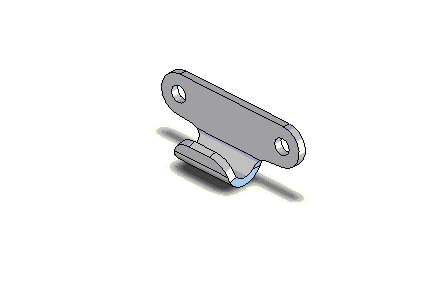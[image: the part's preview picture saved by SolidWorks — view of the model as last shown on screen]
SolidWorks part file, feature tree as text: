
SOLIDWORKS PART (.sldprt)
format: sldprt  version: not decoded by parser v0  size: 239,616 bytes
history: native  units: mm
features: sketch x3, fillet x2, cut_extrude x1, extrude x1 (+11 scaffold rows collapsed)
feature tree (18):
  scaffold x11  (default folders/planes/origin — collapsed)
  sketch  "Sketch1"  dims[c1.D2=5.5mm c1.D3=4.5mm c1.D1=~14.173529mm c2.D1=15.0deg c2.D3=~14.537639mm c2.D4=3.5mm c2.D5=~11.718459mm c3.D3=~14.537639mm c3.D6=~19.037639mm c4.D3=16.5mm c4.D1=40.0mm c4.D5=2.0mm c4.D6=1.0mm c4.D7=5.0mm]
  sketch  "Sketch2"  dims[c1.D1=4.2mm c1.D2=4.2mm c1.D7=2.0mm c2.D2=30.0mm c2.D3=5.0mm c2.D4=16.0mm c2.D5=~12.63534mm c3.D5=80.0deg c4.D5=5.0mm c4.D6=~12.775992mm c5.D6=85.0deg]
  cut_extrude  "Cut-Extrude1"  [1 undecoded]
  fillet  "Fillet3"  Radius=5mm
  sketch  "Sketch3"  dims[c1.D2=~3.422525mm c1.D3=~7.301387mm c1.D4=4.2mm c1.D1=5.0mm c2.D2=30.0mm c2.D3=~7.518114mm c3.D3=5.0deg]
  extrude  "Extrude1"  [1 undecoded]
  fillet  "Fillet4"  Radius=3mm
decode coverage: 5 of 7 modeling features carry decoded parameters
note: ~ marks probable driven/reference dimensions
note: 2 parameter values undecoded
note: suppression state not decoded; provenance and decode notes live in map.json
